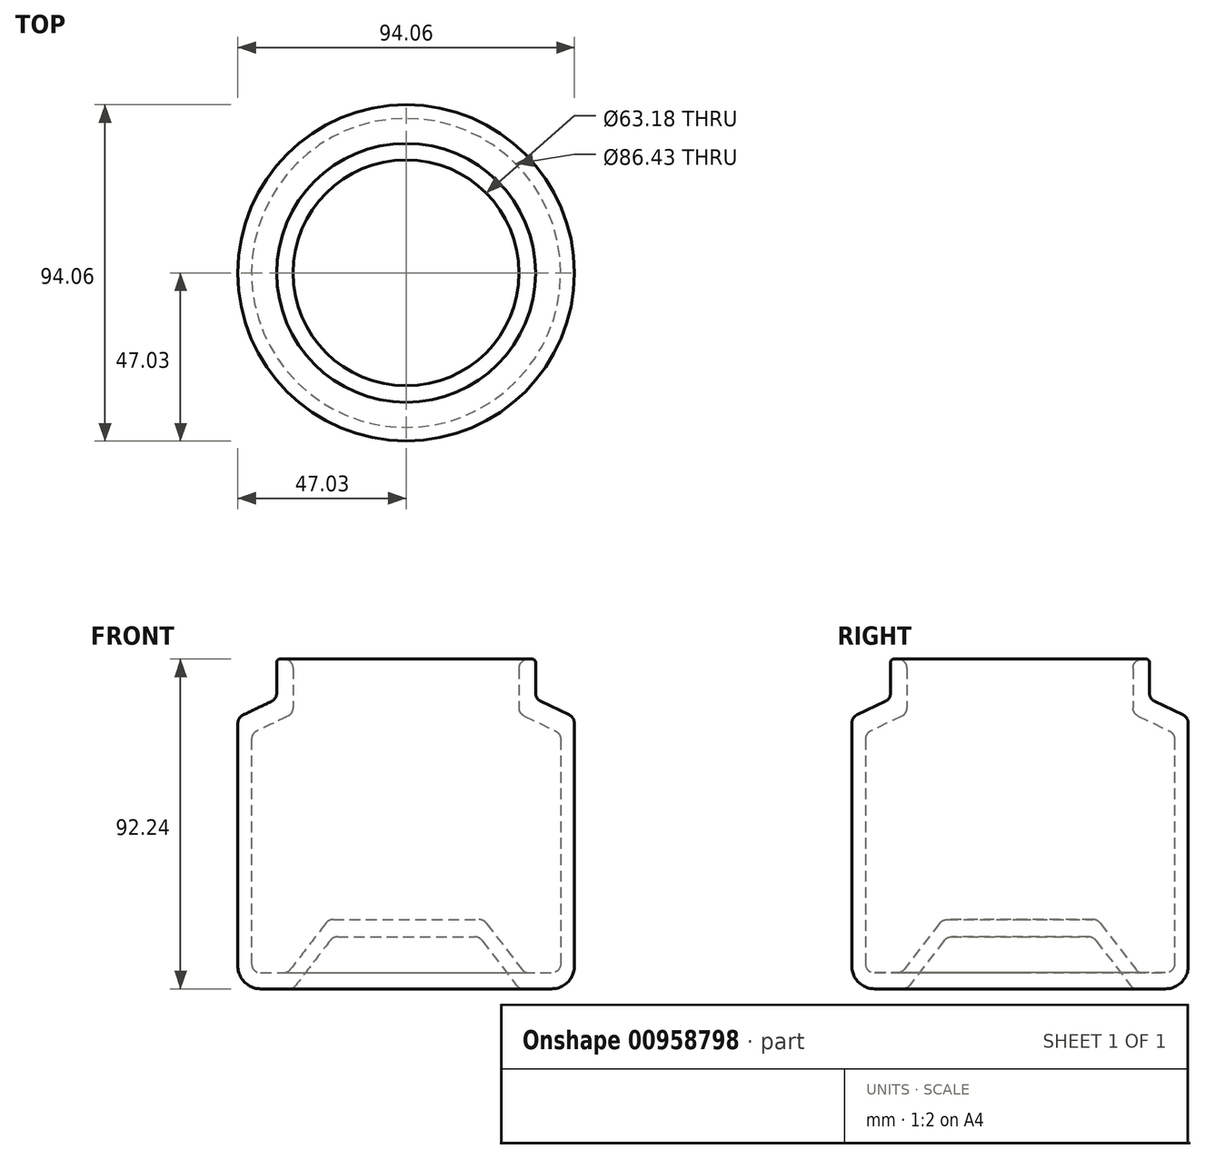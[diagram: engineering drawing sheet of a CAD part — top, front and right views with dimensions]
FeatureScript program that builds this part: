
annotation { "Feature Type Name" : "Feature", "Feature Type Description" : "" }
export const myFeature = defineFeature(function(context is Context, id is Id, definition is map)
    precondition{}
    {
        {
            var Q0;
            Q0=qCreatedBy(makeId("Front.planeOp"),FACE);
            var sketch = newSketch(context, id + "F0", { "sketchPlane" : qUnion([Q0])});
            skLineSegment(sketch, "E0", {"start": v(0, 0) * mm, "end": v(0, 69.96) * mm, "construction": true});
            skLineSegment(sketch, "E1", {"start": v(0, 0) * mm, "end": v(19.2, 0) * mm});
            skLineSegment(sketch, "E2", {"start": v(21.22, -1) * mm, "end": v(30.83, -13.53) * mm});
            skLineSegment(sketch, "E3", {"start": v(32.85, -14.53) * mm, "end": v(40.68, -14.53) * mm});
            skLineSegment(sketch, "E4", {"start": v(47.03, -8.18) * mm, "end": v(47.03, 59.78) * mm});
            skLineSegment(sketch, "E5", {"start": v(45.6, 62.07) * mm, "end": v(37.63, 65.88) * mm});
            skLineSegment(sketch, "E6", {"start": v(36.2, 68.17) * mm, "end": v(36.2, 76.77) * mm});
            skLineSegment(sketch, "E7", {"start": v(35.25, 77.71) * mm, "end": v(34.13, 77.71) * mm});
            skLineSegment(sketch, "E8", {"start": v(31.6, 75.17) * mm, "end": v(31.6, 64.06) * mm});
            skLineSegment(sketch, "E9", {"start": v(33.03, 61.77) * mm, "end": v(41.77, 57.58) * mm});
            skLineSegment(sketch, "E10", {"start": v(43.21, 55.3) * mm, "end": v(43.21, -7.5) * mm});
            skLineSegment(sketch, "E11", {"start": v(40.67, -10.04) * mm, "end": v(34.33, -10.04) * mm});
            skLineSegment(sketch, "E12", {"start": v(32.31, -9.05) * mm, "end": v(22.43, 3.85) * mm});
            skLineSegment(sketch, "E13", {"start": v(20.41, 4.84) * mm, "end": v(0, 4.84) * mm});
            skLineSegment(sketch, "E14", {"start": v(0, 4.84) * mm, "end": v(0, 0) * mm});
            skPoint(sketch, "E15.visualSharp", {"position": v(47.03, -14.53) * mm});
            skArc(sketch, "E15.filletArc", {"start": v(40.68, -14.53) * mm, "mid": v(45.17, -12.67) * mm, "end": v(47.03, -8.18) * mm});
            skPoint(sketch, "E16.visualSharp", {"position": v(43.21, -10.04) * mm});
            skArc(sketch, "E16.filletArc", {"start": v(40.67, -10.04) * mm, "mid": v(42.47, -9.3) * mm, "end": v(43.21, -7.5) * mm});
            skPoint(sketch, "E17.visualSharp", {"position": v(31.6, -14.53) * mm});
            skArc(sketch, "E17.filletArc", {"start": v(30.83, -13.53) * mm, "mid": v(31.72, -14.26) * mm, "end": v(32.85, -14.53) * mm});
            skPoint(sketch, "E18.visualSharp", {"position": v(33.08, -10.04) * mm});
            skArc(sketch, "E18.filletArc", {"start": v(32.31, -9.05) * mm, "mid": v(33.2, -9.78) * mm, "end": v(34.33, -10.04) * mm});
            skPoint(sketch, "E19.visualSharp", {"position": v(20.46, 0) * mm});
            skArc(sketch, "E19.filletArc", {"start": v(21.22, -1) * mm, "mid": v(20.33, -0.26) * mm, "end": v(19.2, 0) * mm});
            skPoint(sketch, "E20.visualSharp", {"position": v(21.67, 4.84) * mm});
            skArc(sketch, "E20.filletArc", {"start": v(22.43, 3.85) * mm, "mid": v(21.54, 4.58) * mm, "end": v(20.41, 4.84) * mm});
            skPoint(sketch, "E21.visualSharp", {"position": v(43.21, 56.9) * mm});
            skArc(sketch, "E21.filletArc", {"start": v(43.21, 55.3) * mm, "mid": v(42.82, 56.64) * mm, "end": v(41.77, 57.58) * mm});
            skPoint(sketch, "E22.visualSharp", {"position": v(47.03, 61.38) * mm});
            skArc(sketch, "E22.filletArc", {"start": v(47.03, 59.78) * mm, "mid": v(46.64, 61.13) * mm, "end": v(45.6, 62.07) * mm});
            skPoint(sketch, "E23.visualSharp", {"position": v(36.2, 66.57) * mm});
            skArc(sketch, "E23.filletArc", {"start": v(36.2, 68.17) * mm, "mid": v(36.58, 66.82) * mm, "end": v(37.63, 65.88) * mm});
            skPoint(sketch, "E24.visualSharp", {"position": v(31.6, 62.46) * mm});
            skArc(sketch, "E24.filletArc", {"start": v(31.6, 64.06) * mm, "mid": v(31.98, 62.7) * mm, "end": v(33.03, 61.77) * mm});
            skPoint(sketch, "E25.visualSharp", {"position": v(31.6, 77.71) * mm});
            skArc(sketch, "E25.filletArc", {"start": v(34.13, 77.71) * mm, "mid": v(32.34, 76.97) * mm, "end": v(31.6, 75.17) * mm});
            skPoint(sketch, "E26.visualSharp", {"position": v(36.2, 77.71) * mm});
            skArc(sketch, "E26.filletArc", {"start": v(36.2, 76.77) * mm, "mid": v(35.92, 77.44) * mm, "end": v(35.25, 77.71) * mm});
            skSolve(sketch);
        }
        {
            var Q0;
            Q0 = qSketchRegion(id + "F0", true);
            var Q1;
            Q1=sQuery(id+"F0.wireOp",EDGE,"E0");
            revolve(context, id + "F1", {"surfaceOperationType" : NewSurfaceOperationType.NEW, "entities" : qUnion([Q0]), "axis" : qUnion([Q1]), "revolveType" : RevolveType.FULL});
        }
    });
